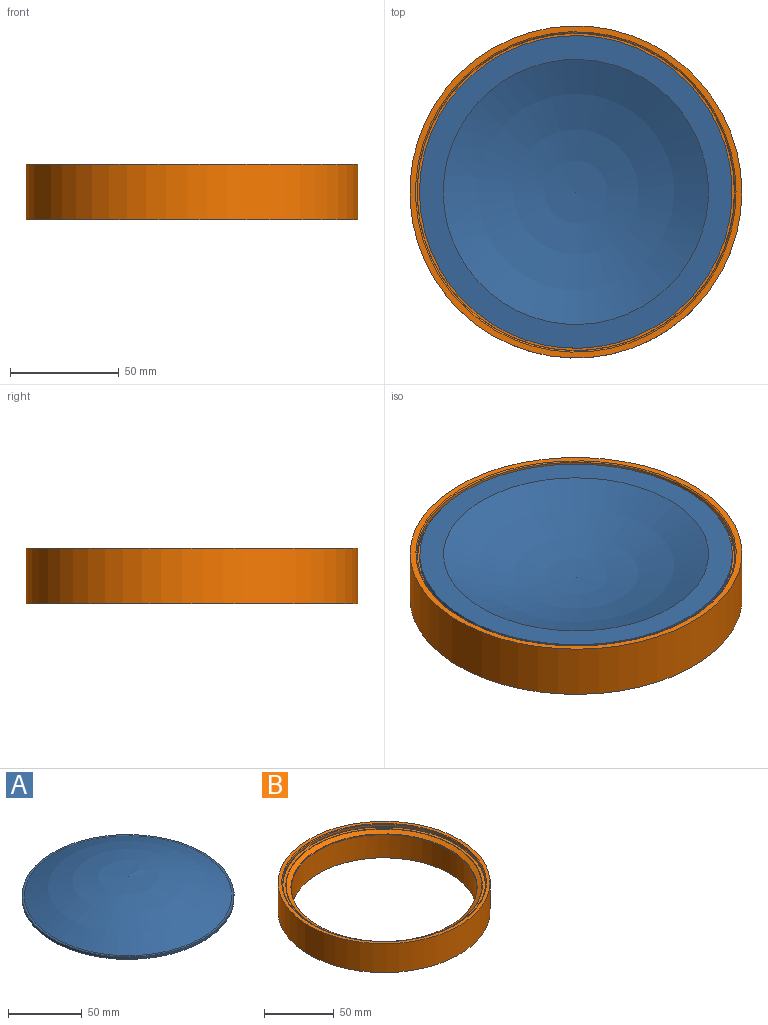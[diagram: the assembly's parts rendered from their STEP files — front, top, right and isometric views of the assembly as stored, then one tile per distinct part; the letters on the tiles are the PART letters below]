
ASSEMBLY  parts=2 mates=1
PART A: 5 faces, bbox 143.5x143.5x18.3 mm
  f0: plane 143.53x143.53mm, normal (0,0,1), area 702.3mm2, adj f1,f4
  f1: cylinder r=71.76mm len=143.53mm, axis (0,0,1), area 881.9mm2, adj f0,f2
  f2: cone r=60.83mm half-angle=89.9deg, axis (0,0,1), area 4553.6mm2, adj f1,f3
  f3: torus R=1.57mm, axis (0,0,1), area 12159.5mm2, adj f2
  f4: torus R=3.66mm, axis (0,0,1), area 16378.4mm2, adj f0
PART B: 11 faces, bbox 159.2x159.2x25.4 mm
  f0: cylinder r=66.67mm len=133.35mm, axis (0,0,1), area 8548.3mm2, adj f3,f9
  f1: cylinder r=76.2mm len=152.4mm, axis (0,0,-1), area 12161mm2, adj f2,f3
  f2: plane 152.4x152.4mm, normal (0,0,1), area 1254.6mm2, adj f1,f7
  f3: plane 152.4x152.4mm, normal (0,0,-1), area 4275.3mm2, adj f0,f1
  f4: plane 145.54x145.54mm, normal (0,0,1), area 969.4mm2, adj f6,f10
  f5: cylinder r=73.03mm len=146.05mm, axis (0,0,1), area 815.8mm2, adj f6,f7
  f6: torus R=72.77mm, axis (0,0,1), area 182.8mm2, adj f4,f5
  f7: torus R=73.53mm, axis (0,0,1), area 367.1mm2, adj f2,f5
  f8: cone r=70.48mm half-angle=60.5deg, axis (0,0,1), area 1703.5mm2, adj f9,f10
  f9: torus R=67.18mm, axis (0,0,-1), area 224.9mm2, adj f0,f8
  f10: torus R=70.62mm, axis (0,0,1), area 116mm2, adj f4,f8
PLACE A rot(axis=(0,1,0),180deg) t=(-10.69,42.5,88.84)mm
PLACE B rot(axis=(-0.92,-0.26,0.28),0deg) t=(-10.69,42.5,64)mm
MATE fastened B.f5 <-> A.f1  axis (0,0,1) through (-10.69,42.5,86.86)mm
